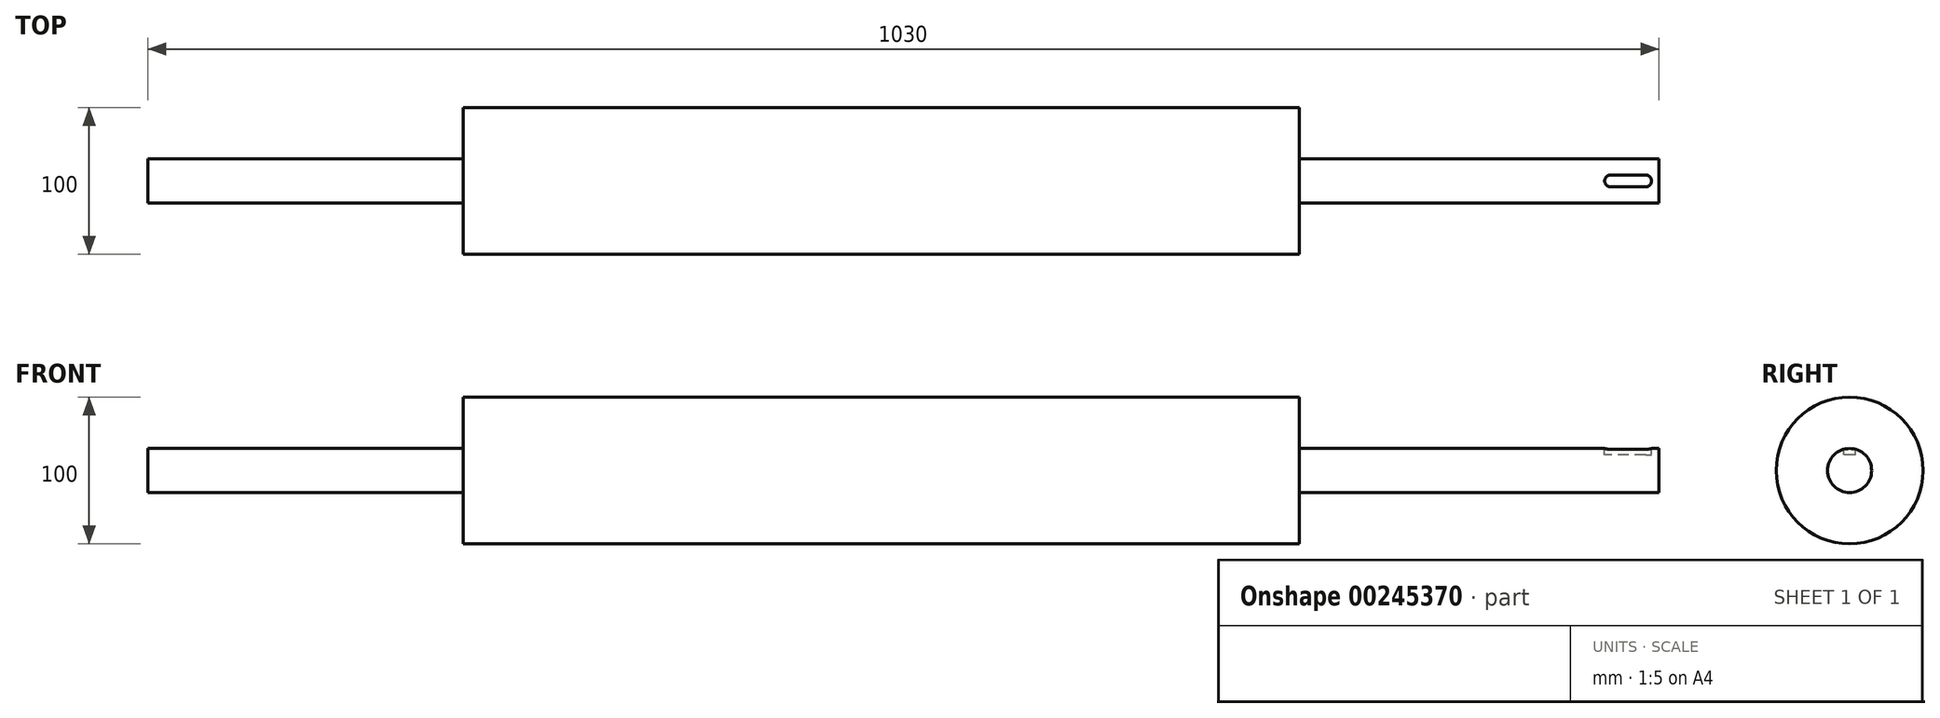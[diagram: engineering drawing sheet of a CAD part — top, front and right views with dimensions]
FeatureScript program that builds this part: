
annotation { "Feature Type Name" : "Feature", "Feature Type Description" : "" }
export const myFeature = defineFeature(function(context is Context, id is Id, definition is map)
    precondition{}
    {
        {
            var Q0;
            Q0=qCreatedBy(makeId("Right.planeOp"),FACE);
            var sketch = newSketch(context, id + "F0", { "sketchPlane" : qUnion([Q0])});
            skCircle(sketch, "E0", {"center": v(0, 0) * mm, "radius": 50 * mm});
            skSolve(sketch);
        }
        {
            var Q0;
            Q0=makeQuery(id+"F0.imprint","IMPRINT",FACE,{"disambiguationData":[TD([[makeQuery(id+"F0.imprint","IMPRINT",EDGE,{"derivedFrom":sQuery(id+"F0.wireOp",EDGE,"E0")}),1.0]])]});
            extrude(context, id + "F1", {"entities" : qUnion([Q0]), "depth" : 570 * mm});
        }
        {
            var Q0;
            Q0=makeQuery(id+"F1.opExtrude","CAP_FACE",FACE,{"disambiguationData":[OSD([sQuery(id+"F0.wireOp",EDGE,"E0")])],"isStart":true});
            var sketch = newSketch(context, id + "F2", { "sketchPlane" : qUnion([Q0])});
            skCircle(sketch, "E1", {"center": v(0, 0) * mm, "radius": 15 * mm});
            skSolve(sketch);
        }
        {
            var Q0;
            Q0=makeQuery(id+"F2.imprint","IMPRINT",FACE,{"disambiguationData":[TD([[makeQuery(id+"F2.imprint","IMPRINT",EDGE,{"derivedFrom":sQuery(id+"F2.wireOp",EDGE,"E1")}),1.0]])]});
            extrude(context, id + "F3", {"entities" : qUnion([Q0]), "operationType" : NewBodyOperationType.ADD, "depth" : 215 * mm});
        }
        {
            var Q0;
            Q0=makeQuery(id+"F1.opExtrude","CAP_FACE",FACE,{"disambiguationData":[OSD([sQuery(id+"F0.wireOp",EDGE,"E0")])],"isStart":false});
            var sketch = newSketch(context, id + "F4", { "sketchPlane" : qUnion([Q0])});
            skCircle(sketch, "E2", {"center": v(0, 0) * mm, "radius": 15 * mm});
            skSolve(sketch);
        }
        {
            var Q0;
            Q0=makeQuery(id+"F4.imprint","IMPRINT",FACE,{"disambiguationData":[TD([[makeQuery(id+"F4.imprint","IMPRINT",EDGE,{"derivedFrom":sQuery(id+"F4.wireOp",EDGE,"E2")}),1.0]])]});
            extrude(context, id + "F5", {"entities" : qUnion([Q0]), "operationType" : NewBodyOperationType.ADD, "depth" : 245 * mm});
        }
        {
            var Q0;
            Q0=qCreatedBy(makeId("Top.planeOp"),FACE);
            cPlane(context, id + "F6", {"entities" : qUnion([Q0]), "cplaneType" : CPlaneType.OFFSET, "offset" : 15 * mm, "width" : 150 * mm, "height" : 150 * mm});
        }
        {
            var Q0;
            Q0=qCreatedBy(id+"F6.planeOp",FACE);
            var sketch = newSketch(context, id + "F7", { "sketchPlane" : qUnion([Q0])});
            skLineSegment(sketch, "E3", {"start": v(810, 0) * mm, "end": v(810, 0) * mm});
            skLineSegment(sketch, "E4", {"start": v(806, 4) * mm, "end": v(782, 4) * mm});
            skLineSegment(sketch, "E5", {"start": v(806, -4) * mm, "end": v(782, -4) * mm});
            skLineSegment(sketch, "E6", {"start": v(778, 0) * mm, "end": v(778, 0) * mm});
            skPoint(sketch, "E7.visualSharp", {"position": v(778, 4) * mm});
            skArc(sketch, "E7.filletArc", {"start": v(782, 4) * mm, "mid": v(779.17, 2.83) * mm, "end": v(778, 0) * mm});
            skPoint(sketch, "E8.visualSharp", {"position": v(778, -4) * mm});
            skArc(sketch, "E8.filletArc", {"start": v(778, 0) * mm, "mid": v(779.17, -2.83) * mm, "end": v(782, -4) * mm});
            skPoint(sketch, "E9.visualSharp", {"position": v(810, 4) * mm});
            skArc(sketch, "E9.filletArc", {"start": v(810, 0) * mm, "mid": v(808.83, 2.83) * mm, "end": v(806, 4) * mm});
            skPoint(sketch, "E10.visualSharp", {"position": v(810, -4) * mm});
            skArc(sketch, "E10.filletArc", {"start": v(806, -4) * mm, "mid": v(808.83, -2.83) * mm, "end": v(810, 0) * mm});
            skSolve(sketch);
        }
        {
            var Q0;
            Q0=makeQuery(id+"F7.imprint","IMPRINT",FACE,{"disambiguationData":[TD([[makeQuery(id+"F7.imprint","IMPRINT",EDGE,{"derivedFrom":sQuery(id+"F7.wireOp",EDGE,"E4")}),1.0]])]});
            extrude(context, id + "F8", {"entities" : qUnion([Q0]), "operationType" : NewBodyOperationType.REMOVE, "oppositeDirection" : true, "depth" : 4.5 * mm});
        }
    });
